# Revit family: Life-allas
name_source: partatom
category: Plumbing Fixtures
revit_build: Autodesk Revit 2015 (Build: 20160512_0715(x64)
units: mm (PartAtom-declared; Revit-internal decimal feet)

## types (3) — shared parameters
Assembly Code = 1336
Assembly Height = 800 mm  [stored 2.62467 ft]
Colour = White Porcelain
Depth = 400 mm  [stored 1.31234 ft]
Height = 90 mm  [stored 0.295276 ft]
Keynote = 523
Manufacturer = Väinö Korpinen Oy
Model = Life
Thickness = 30 mm  [stored 0.0984252 ft]
Width = 600 mm  [stored 1.9685 ft]

## per-type parameters (varying)
| type | Sink Type |
| 6700 | Life-allas 6700_6721_6722 : 6700 |
| 6721 | Life-allas 6700_6721_6722 : 6721 |
| 6722 | Life-allas 6700_6721_6722 : 6722 |

note: column(s) folded — value = type name in every type: Model ID

note: [stored X ft] marks values corroborated as IEEE doubles in the binary element streams (Revit-internal decimal feet)

## geometry (parser evidence)
native form markers: Blend x4, Sweep x8
no freeform markers — native parametric forms only
